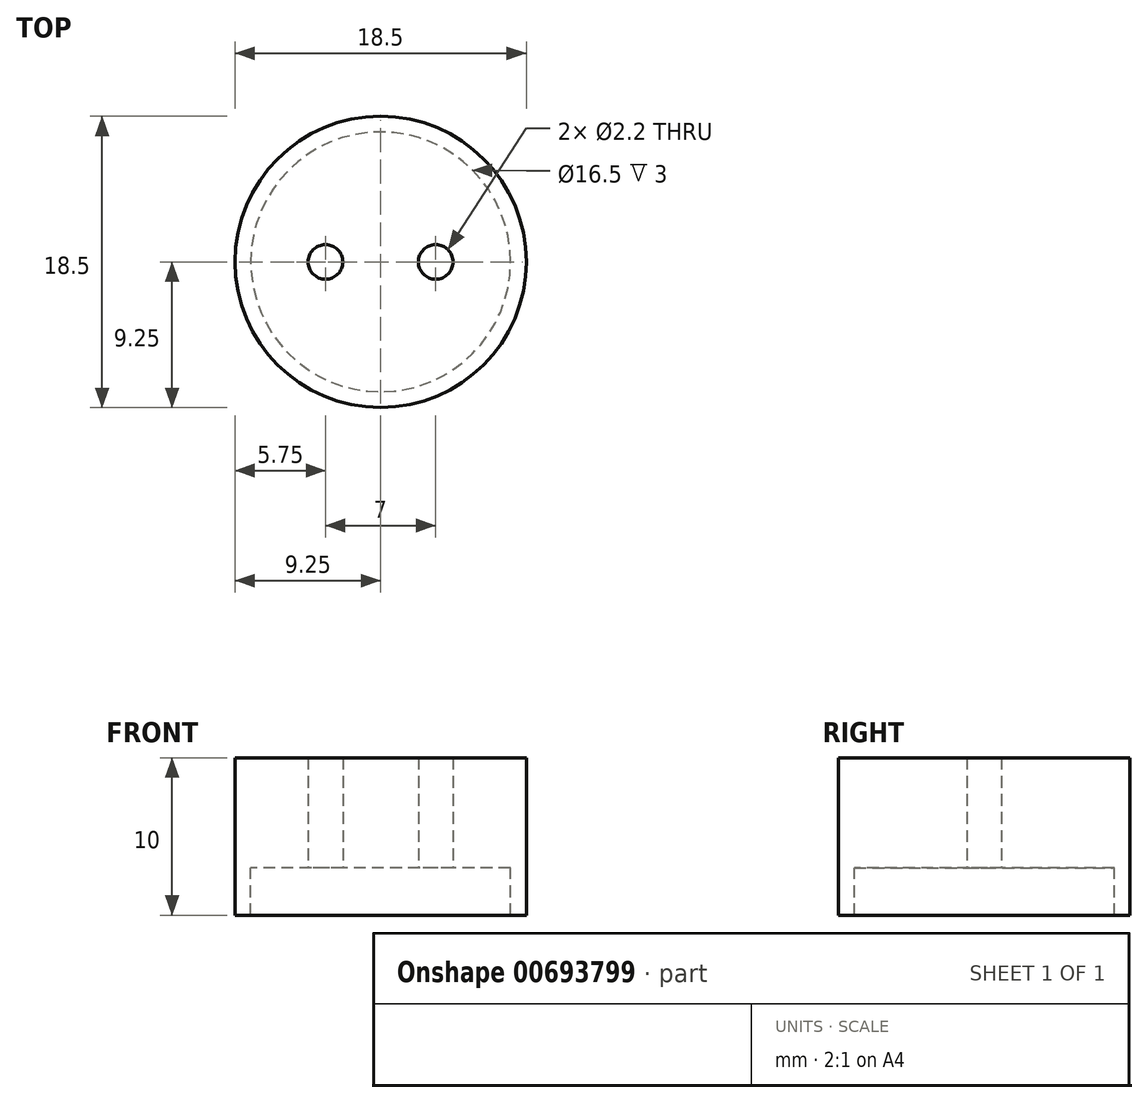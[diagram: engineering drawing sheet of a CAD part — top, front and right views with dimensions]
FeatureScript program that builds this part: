
annotation { "Feature Type Name" : "Feature", "Feature Type Description" : "" }
export const myFeature = defineFeature(function(context is Context, id is Id, definition is map)
    precondition{}
    {
        {
            var Q0;
            Q0=qCreatedBy(makeId("Top.planeOp"),FACE);
            var sketch = newSketch(context, id + "F0", { "sketchPlane" : qUnion([Q0])});
            skCircle(sketch, "E0", {"center": v(0, 0) * mm, "radius": 8.25 * mm});
            skCircle(sketch, "E1", {"center": v(0, 0) * mm, "radius": 9.25 * mm});
            skCircle(sketch, "E2", {"center": v(-3.5, 0) * mm, "radius": 1.1 * mm});
            skCircle(sketch, "E3.MirrorC", {"center": v(3.5, 0) * mm, "radius": 1.1 * mm});
            skSolve(sketch);
        }
        {
            var Q0;
            Q0=makeQuery(id+"F0.imprint","IMPRINT",FACE,{"disambiguationData":[TD([[makeQuery(id+"F0.imprint","IMPRINT",EDGE,{"derivedFrom":sQuery(id+"F0.wireOp",EDGE,"E0")}),1.0]])]});
            var Q1;
            Q1=makeQuery(id+"F0.imprint","IMPRINT",FACE,{"disambiguationData":[TD([[makeQuery(id+"F0.imprint","IMPRINT",EDGE,{"derivedFrom":sQuery(id+"F0.wireOp",EDGE,"E0")}),-1.0]])]});
            extrude(context, id + "F1", {"entities" : qUnion([Q0, Q1]), "depth" : 7 * mm, "offsetDistance" : 25 * mm});
        }
        {
            var Q0;
            Q0=makeQuery(id+"F0.imprint","IMPRINT",FACE,{"disambiguationData":[TD([[makeQuery(id+"F0.imprint","IMPRINT",EDGE,{"derivedFrom":sQuery(id+"F0.wireOp",EDGE,"E0")}),-1.0]])]});
            extrude(context, id + "F2", {"entities" : qUnion([Q0]), "operationType" : NewBodyOperationType.ADD, "oppositeDirection" : true, "depth" : 3 * mm, "offsetDistance" : 25 * mm});
        }
    });
